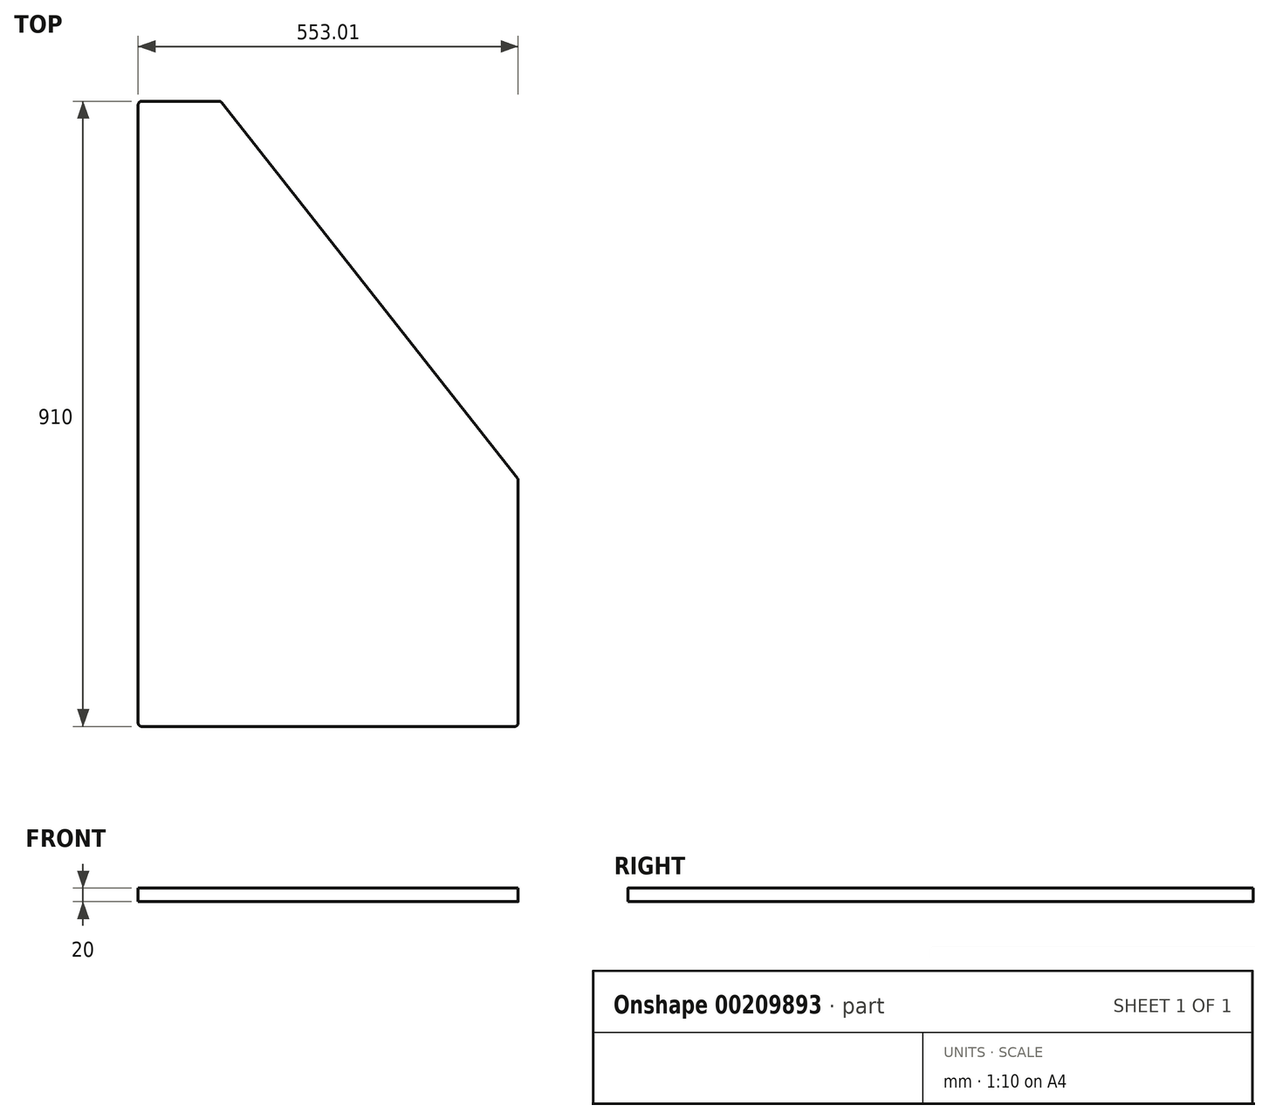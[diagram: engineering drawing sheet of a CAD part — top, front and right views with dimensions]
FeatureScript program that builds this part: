
annotation { "Feature Type Name" : "Feature", "Feature Type Description" : "" }
export const myFeature = defineFeature(function(context is Context, id is Id, definition is map)
    precondition{}
    {
        {
            var Q0;
            Q0=qCreatedBy(makeId("Top.planeOp"),FACE);
            var sketch = newSketch(context, id + "F0", { "sketchPlane" : qUnion([Q0])});
            skLineSegment(sketch, "E0", {"start": v(-307.42, 382.37) * mm, "end": v(-307.42, -527.63) * mm});
            skLineSegment(sketch, "E1", {"start": v(-307.42, 382.37) * mm, "end": v(-207.42, 382.37) * mm});
            skLineSegment(sketch, "E2", {"start": v(-307.42, -527.63) * mm, "end": v(245.6, -527.63) * mm});
            skLineSegment(sketch, "E3", {"start": v(245.6, -527.63) * mm, "end": v(245.6, -167.63) * mm});
            skLineSegment(sketch, "E4", {"start": v(245.6, -167.63) * mm, "end": v(-187.42, 382.37) * mm});
            skLineSegment(sketch, "E5", {"start": v(-207.42, 382.37) * mm, "end": v(-187.42, 382.37) * mm});
            skSolve(sketch);
        }
        {
            var Q0;
            Q0=makeQuery(id+"F0.imprint","IMPRINT",FACE,{"disambiguationData":[TD([[makeQuery(id+"F0.imprint","IMPRINT",EDGE,{"derivedFrom":sQuery(id+"F0.wireOp",EDGE,"E0")}),1.0]])]});
            extrude(context, id + "F1", {"entities" : qUnion([Q0]), "depth" : 20 * mm});
        }
        {
            var Q0;
            Q0=makeQuery(id+"F1.opExtrude","SWEPT_EDGE",EDGE,{"disambiguationData":[OSD([sQuery(id+"F0.wireOp",EDGE,"E3"),sQuery(id+"F0.wireOp",EDGE,"E4")])]});
            var Q1;
            Q1=makeQuery(id+"F1.opExtrude","SWEPT_EDGE",EDGE,{"disambiguationData":[OSD([sQuery(id+"F0.wireOp",EDGE,"E2"),sQuery(id+"F0.wireOp",EDGE,"E3")])]});
            var Q2;
            Q2=makeQuery(id+"F1.opExtrude","SWEPT_EDGE",EDGE,{"disambiguationData":[OSD([sQuery(id+"F0.wireOp",EDGE,"E4"),sQuery(id+"F0.wireOp",EDGE,"E5")])]});
            var Q3;
            Q3=makeQuery(id+"F1.opExtrude","SWEPT_EDGE",EDGE,{"disambiguationData":[OSD([sQuery(id+"F0.wireOp",EDGE,"E0"),sQuery(id+"F0.wireOp",EDGE,"E2")])]});
            var Q4;
            Q4=makeQuery(id+"F1.opExtrude","SWEPT_EDGE",EDGE,{"disambiguationData":[OSD([sQuery(id+"F0.wireOp",EDGE,"E0"),sQuery(id+"F0.wireOp",EDGE,"E1")])]});
            fillet(context, id + "F2", {"entities" : qUnion([Q0, Q1, Q2, Q3, Q4]), "radius" : 5 * mm, "tangentPropagation" : true, "allowEdgeOverflow" : false});
        }
    });
